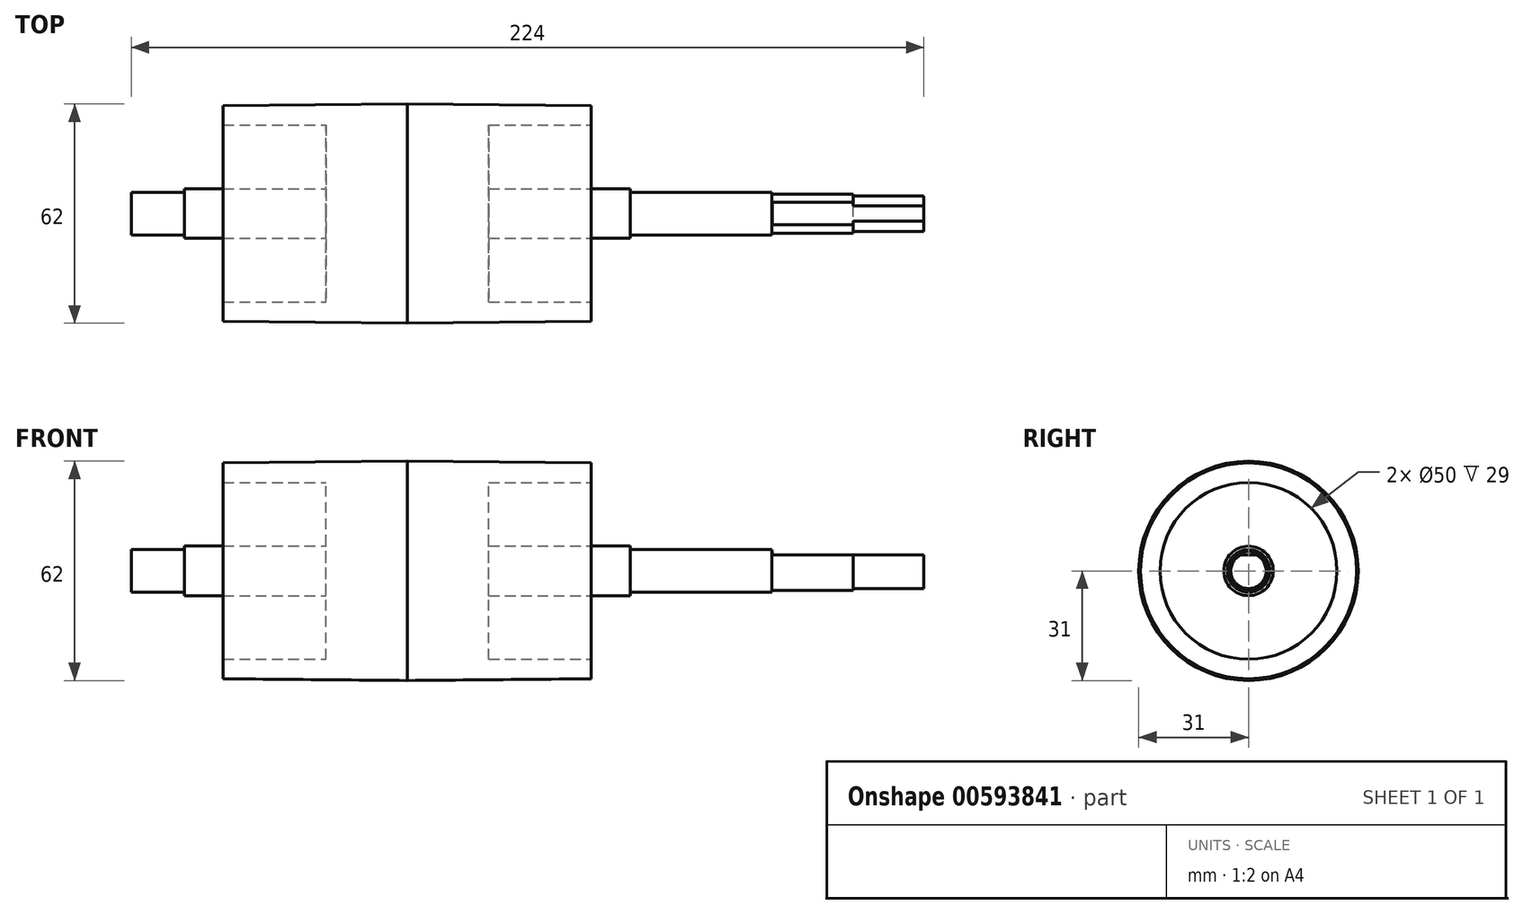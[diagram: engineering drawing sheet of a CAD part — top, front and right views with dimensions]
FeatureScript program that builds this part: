
annotation { "Feature Type Name" : "Feature", "Feature Type Description" : "" }
export const myFeature = defineFeature(function(context is Context, id is Id, definition is map)
    precondition{}
    {
        {
            var Q0;
            Q0=qCreatedBy(makeId("Front.planeOp"),FACE);
            var sketch = newSketch(context, id + "F0", { "sketchPlane" : qUnion([Q0])});
            skLineSegment(sketch, "E0", {"start": v(-52.79, 0) * mm, "end": v(-52.79, 6) * mm});
            skLineSegment(sketch, "E1", {"start": v(-52.79, 6) * mm, "end": v(-37.79, 6) * mm});
            skLineSegment(sketch, "E2", {"start": v(-37.79, 6) * mm, "end": v(-37.79, 7) * mm});
            skLineSegment(sketch, "E3", {"start": v(-37.79, 7) * mm, "end": v(2.21, 7) * mm});
            skLineSegment(sketch, "E4", {"start": v(2.21, 7) * mm, "end": v(2.21, 25) * mm});
            skLineSegment(sketch, "E5", {"start": v(2.21, 25) * mm, "end": v(-26.79, 25) * mm});
            skLineSegment(sketch, "E6", {"start": v(-26.79, 25) * mm, "end": v(-26.79, 30.5) * mm});
            skPoint(sketch, "E7", {"position": v(25.21, 0) * mm});
            skPoint(sketch, "E8", {"position": v(25.21, 31) * mm});
            skPoint(sketch, "E9", {"position": v(77.21, 30.5) * mm});
            skLineSegment(sketch, "E10", {"start": v(-26.79, 30.5) * mm, "end": v(25.21, 31) * mm});
            skLineSegment(sketch, "E11", {"start": v(25.21, 31) * mm, "end": v(77.21, 30.5) * mm});
            skLineSegment(sketch, "E12", {"start": v(77.21, 30.5) * mm, "end": v(77.21, 25) * mm});
            skLineSegment(sketch, "E13", {"start": v(77.21, 25) * mm, "end": v(48.21, 25) * mm});
            skLineSegment(sketch, "E14", {"start": v(48.21, 25) * mm, "end": v(48.21, 7) * mm});
            skLineSegment(sketch, "E15", {"start": v(48.21, 7) * mm, "end": v(88.21, 7) * mm});
            skLineSegment(sketch, "E16", {"start": v(88.21, 7) * mm, "end": v(88.21, 6) * mm});
            skLineSegment(sketch, "E17", {"start": v(88.21, 6) * mm, "end": v(128.21, 6) * mm});
            skLineSegment(sketch, "E18", {"start": v(128.21, 6) * mm, "end": v(128.21, 5.5) * mm});
            skLineSegment(sketch, "E19", {"start": v(128.21, 5.5) * mm, "end": v(151.21, 5.5) * mm});
            skLineSegment(sketch, "E20", {"start": v(151.21, 5.5) * mm, "end": v(151.21, 5) * mm});
            skLineSegment(sketch, "E21", {"start": v(151.21, 5) * mm, "end": v(171.21, 5) * mm});
            skLineSegment(sketch, "E22", {"start": v(171.21, 5) * mm, "end": v(171.21, 0) * mm});
            skLineSegment(sketch, "E23", {"start": v(171.21, 0) * mm, "end": v(-52.79, 0) * mm});
            skSolve(sketch);
        }
        {
            var Q0;
            Q0=makeQuery(id+"F0.imprint","IMPRINT",FACE,{"disambiguationData":[TD([[makeQuery(id+"F0.imprint","IMPRINT",EDGE,{"derivedFrom":sQuery(id+"F0.wireOp",EDGE,"E0")}),-1.0]])]});
            var Q1;
            Q1=sQuery(id+"F0.wireOp",EDGE,"E23");
            revolve(context, id + "F1", {"entities" : qUnion([Q0]), "axis" : qUnion([Q1]), "revolveType" : RevolveType.FULL});
        }
        {
            var Q0;
            Q0=qCreatedBy(makeId("Top.planeOp"),FACE);
            cPlane(context, id + "F2", {"entities" : qUnion([Q0]), "cplaneType" : CPlaneType.OFFSET, "offset" : 5.5 * mm, "width" : 150 * mm, "height" : 150 * mm});
        }
        {
            var Q0;
            Q0=makeQuery(id+"F1.opRevolve","SWEPT_BODY",BODY,{"disambiguationData":[OSD([sQuery(id+"F0.wireOp",EDGE,"E0"),sQuery(id+"F0.wireOp",EDGE,"E1"),sQuery(id+"F0.wireOp",EDGE,"E2"),sQuery(id+"F0.wireOp",EDGE,"E3"),sQuery(id+"F0.wireOp",EDGE,"E4"),sQuery(id+"F0.wireOp",EDGE,"E5"),sQuery(id+"F0.wireOp",EDGE,"E6"),sQuery(id+"F0.wireOp",EDGE,"E10"),sQuery(id+"F0.wireOp",EDGE,"E11"),sQuery(id+"F0.wireOp",EDGE,"E12"),sQuery(id+"F0.wireOp",EDGE,"E13"),sQuery(id+"F0.wireOp",EDGE,"E14"),sQuery(id+"F0.wireOp",EDGE,"E15"),sQuery(id+"F0.wireOp",EDGE,"E16"),sQuery(id+"F0.wireOp",EDGE,"E17"),sQuery(id+"F0.wireOp",EDGE,"E18"),sQuery(id+"F0.wireOp",EDGE,"E19"),sQuery(id+"F0.wireOp",EDGE,"E20"),sQuery(id+"F0.wireOp",EDGE,"E21"),sQuery(id+"F0.wireOp",EDGE,"E22"),sQuery(id+"F0.wireOp",EDGE,"E23")])]});
            transform(context, id + "F3", {"entities" : qUnion([Q0]), "transformType" : TransformType.TRANSLATION_3D, "dx" : -70 * mm, "dy" : 0 * mm, "dz" : 0 * mm, "makeCopy" : false});
        }
        {
            var Q0;
            Q0=qCreatedBy(id+"F2.planeOp",FACE);
            var sketch = newSketch(context, id + "F4", { "sketchPlane" : qUnion([Q0])});
            skLineSegment(sketch, "E24.bottom", {"start": v(101.7, -5.55) * mm, "end": v(58.31, -5.55) * mm});
            skLineSegment(sketch, "E24.top", {"start": v(101.7, 5.59) * mm, "end": v(58.31, 5.59) * mm});
            skLineSegment(sketch, "E24.left", {"start": v(101.7, -5.55) * mm, "end": v(101.7, 5.59) * mm});
            skLineSegment(sketch, "E24.right", {"start": v(58.31, -5.55) * mm, "end": v(58.31, 5.59) * mm});
            skSolve(sketch);
        }
        {
            var Q0;
            Q0=makeQuery(id+"F4.imprint","IMPRINT",FACE,{"disambiguationData":[TD([[makeQuery(id+"F4.imprint","IMPRINT",EDGE,{"derivedFrom":sQuery(id+"F4.wireOp",EDGE,"E24.bottom")}),-1.0]])]});
            extrude(context, id + "F5", {"entities" : qUnion([Q0]), "operationType" : NewBodyOperationType.REMOVE, "oppositeDirection" : true, "depth" : 1 * mm, "offsetDistance" : 25 * mm});
        }
    });
